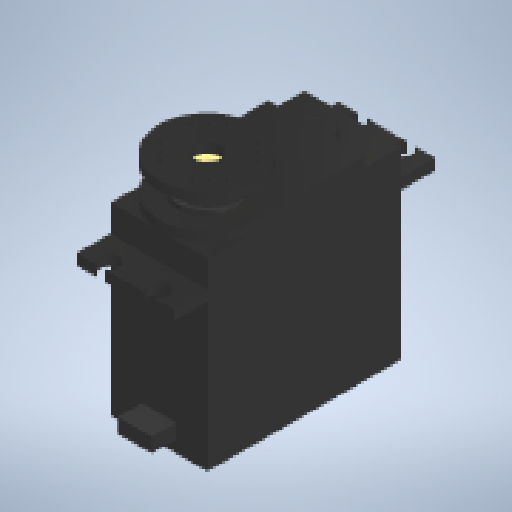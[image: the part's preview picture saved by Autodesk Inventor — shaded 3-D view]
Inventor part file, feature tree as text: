
AUTODESK INVENTOR PART (.ipt)
format: ipt  version: 2025.2 (Build 292293000, 293)  size: 332,800 bytes
history: native  units: mm
features: extrude x3, other x2, sketch x1, pattern_circular x1
ambient origin geometry x8: Origin, YZ Plane, XZ Plane, XY Plane, X Axis, Y Axis, Z Axis, Center Point
bodies: Body1 (feature_tree)
feature tree (7):
  other  "Sólido1"
  sketch  "Esboço1"  dims[d0=20.0mm d1=2.0mm d2=0.0mm d3=45.0deg d4=1.0mm d5=5.0mm d6=5.0mm d7=90.0deg d8=0.0mm d9=0.0mm d10=40.0mm d11=360.0deg d13=5.05mm d14=2.0mm d15=0.0mm d16=0.5mm d17=0.872665mm]
  extrude  "Extrusão1"  Depth=2.0mm TaperAngle=0.0deg
  extrude  "Extrusão2"  TaperAngle=45.0deg  [1 undecoded]
  pattern_circular  "Padrão circular1"  [2 undecoded]
  extrude  "Extrusão3"  Depth=5.0mm
  other  "Cut-Extrude2"
note: 3 required parameter values undecoded (feature->parameter linkage not recoverable at this tier; creation-order binding heuristic only, values carry confidence <= 0.55)
